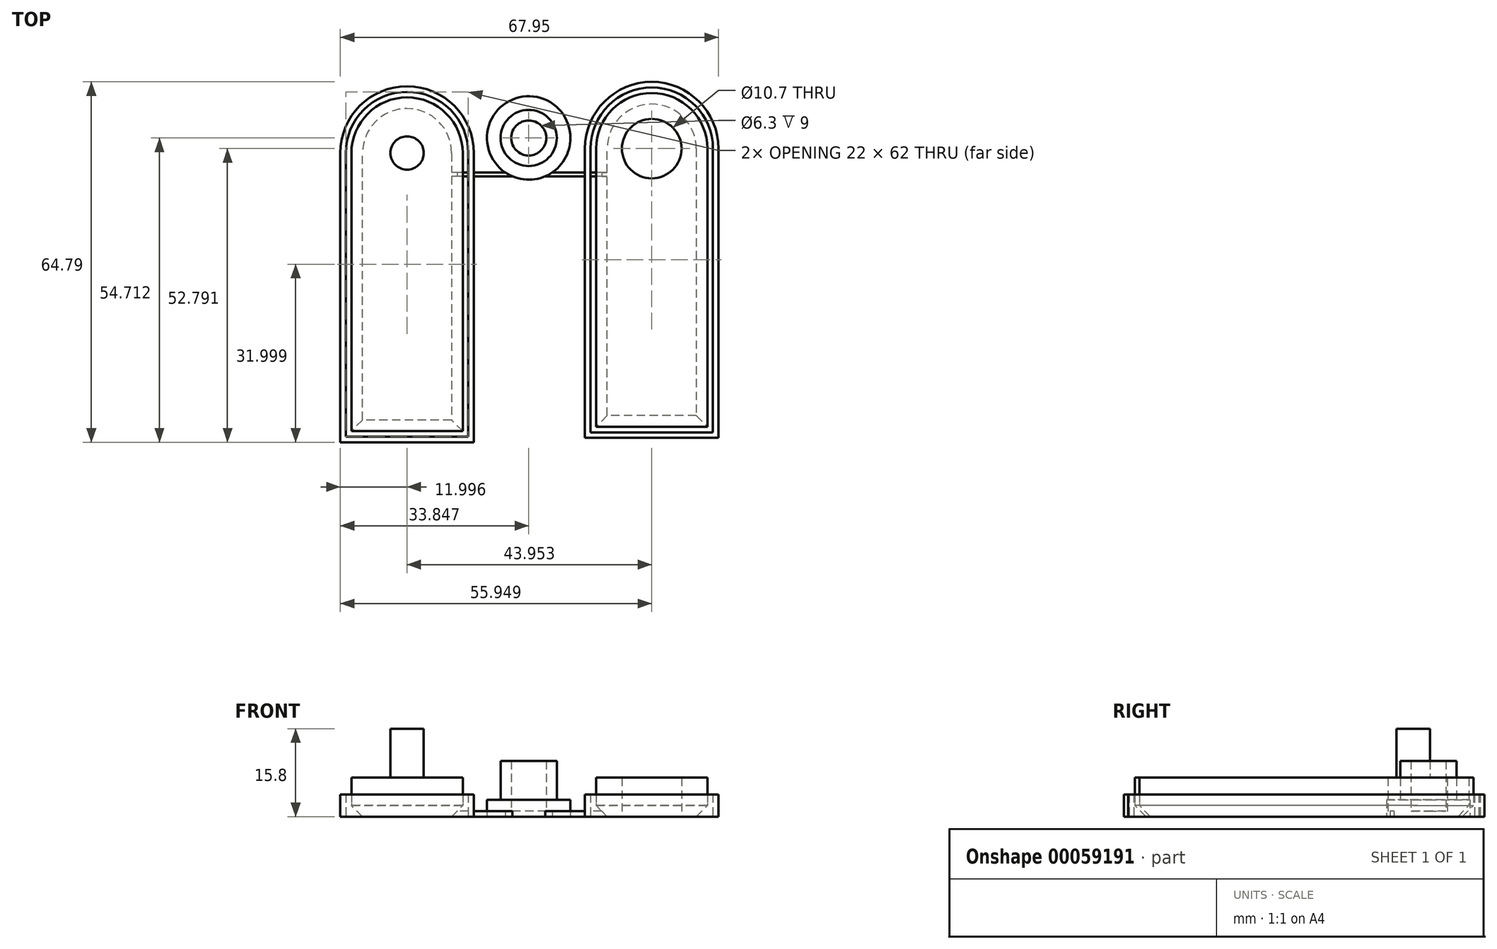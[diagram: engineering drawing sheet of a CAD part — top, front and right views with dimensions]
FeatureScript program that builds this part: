
annotation { "Feature Type Name" : "Feature", "Feature Type Description" : "" }
export const myFeature = defineFeature(function(context is Context, id is Id, definition is map)
    precondition{}
    {
        {
            assignVariable(context, id + "F0", {"name" : "heatWallThickness", "anyValue" : 4});
        }
        {
            var Q0;
            Q0=qCreatedBy(makeId("Top.planeOp"),FACE);
            var sketch = newSketch(context, id + "F1", { "sketchPlane" : qUnion([Q0])});
            skLineSegment(sketch, "E0.top", {"start": v(-67.54, 9.8) * mm, "end": v(-47.54, 9.8) * mm});
            skLineSegment(sketch, "E0.left", {"start": v(-67.54, 59.8) * mm, "end": v(-67.54, 9.8) * mm});
            skLineSegment(sketch, "E0.right", {"start": v(-47.54, 59.8) * mm, "end": v(-47.54, 9.8) * mm});
            skArc(sketch, "E1", {"start": v(-47.54, 59.8) * mm, "mid": v(-57.54, 69.8) * mm, "end": v(-67.54, 59.8) * mm});
            skCircle(sketch, "E2", {"center": v(-57.54, 59.8) * mm, "radius": 3 * mm});
            skLineSegment(sketch, "E3.left", {"start": v(-23.6, 60.6) * mm, "end": v(-23.6, 10.6) * mm});
            skCircle(sketch, "E4", {"center": v(-13.6, 60.6) * mm, "radius": 5.35 * mm});
            skArc(sketch, "E5", {"start": v(-3.6, 60.6) * mm, "mid": v(-13.6, 70.6) * mm, "end": v(-23.6, 60.6) * mm});
            skLineSegment(sketch, "E3.right", {"start": v(-3.6, 60.6) * mm, "end": v(-3.6, 10.6) * mm});
            skLineSegment(sketch, "E3.top", {"start": v(-23.6, 10.6) * mm, "end": v(-3.6, 10.6) * mm});
            skCircle(sketch, "E6", {"center": v(-35.7, 62.51) * mm, "radius": 7.5 * mm});
            skCircle(sketch, "E7", {"center": v(-35.7, 62.51) * mm, "radius": 5.05 * mm});
            skCircle(sketch, "E8", {"center": v(-35.7, 62.51) * mm, "radius": 3.15 * mm});
            skLineSegment(sketch, "E9.0", {"start": v(-46.54, 59.8) * mm, "end": v(-46.54, 8.8) * mm});
            skArc(sketch, "E9.1", {"start": v(-46.54, 59.8) * mm, "mid": v(-57.54, 70.8) * mm, "end": v(-68.54, 59.8) * mm});
            skLineSegment(sketch, "E9.2", {"start": v(-68.54, 59.8) * mm, "end": v(-68.54, 8.8) * mm});
            skLineSegment(sketch, "E9.3", {"start": v(-68.54, 8.8) * mm, "end": v(-46.54, 8.8) * mm});
            skLineSegment(sketch, "E10.0", {"start": v(-69.54, 7.8) * mm, "end": v(-45.54, 7.8) * mm});
            skLineSegment(sketch, "E10.1", {"start": v(-69.54, 59.8) * mm, "end": v(-69.54, 7.8) * mm});
            skArc(sketch, "E10.2", {"start": v(-45.54, 59.8) * mm, "mid": v(-57.54, 71.8) * mm, "end": v(-69.54, 59.8) * mm});
            skLineSegment(sketch, "E10.3", {"start": v(-45.54, 59.8) * mm, "end": v(-45.54, 7.8) * mm});
            skLineSegment(sketch, "E11.0", {"start": v(-24.6, 9.6) * mm, "end": v(-2.6, 9.6) * mm});
            skLineSegment(sketch, "E11.1", {"start": v(-24.6, 60.6) * mm, "end": v(-24.6, 9.6) * mm});
            skArc(sketch, "E11.2", {"start": v(-2.6, 60.6) * mm, "mid": v(-13.6, 71.6) * mm, "end": v(-24.6, 60.6) * mm});
            skLineSegment(sketch, "E11.3", {"start": v(-2.6, 60.6) * mm, "end": v(-2.6, 9.6) * mm});
            skLineSegment(sketch, "E12.0", {"start": v(-25.6, 8.6) * mm, "end": v(-1.6, 8.6) * mm});
            skLineSegment(sketch, "E12.1", {"start": v(-25.6, 60.6) * mm, "end": v(-25.6, 8.6) * mm});
            skArc(sketch, "E12.2", {"start": v(-1.6, 60.6) * mm, "mid": v(-13.6, 72.6) * mm, "end": v(-25.6, 60.6) * mm});
            skLineSegment(sketch, "E12.3", {"start": v(-1.6, 60.6) * mm, "end": v(-1.6, 8.6) * mm});
            skSolve(sketch);
        }
        {
            assignVariable(context, id + "F2", {"name" : "thickness", "anyValue" : 7 * mm});
        }
        {
            assignVariable(context, id + "F3", {"name" : "knobThickness", "anyValue" : 3 * mm});
        }
        {
            assignVariable(context, id + "F4", {"name" : "chamfer", "anyValue" : 2});
        }
        {
            var Q0;
            Q0=makeQuery(id+"F1.imprint","IMPRINT",FACE,{"disambiguationData":[TD([[makeQuery(id+"F1.imprint","IMPRINT",EDGE,{"derivedFrom":sQuery(id+"F1.wireOp",EDGE,"E0.top")}),1.0]])]});
            extrude(context, id + "F5", {"entities" : qUnion([Q0]), "depth" : getVariable(context, 'thickness')});
        }
        {
            var Q0;
            Q0=makeQuery(id+"F5.opExtrude","CAP_EDGE",EDGE,{"disambiguationData":[OSD([sQuery(id+"F1.wireOp",EDGE,"E0.top")])],"isStart":true});
            var Q1;
            Q1=makeQuery(id+"F5.opExtrude","CAP_EDGE",EDGE,{"disambiguationData":[OSD([sQuery(id+"F1.wireOp",EDGE,"E0.right")])],"isStart":true});
            var Q2;
            Q2=makeQuery(id+"F5.opExtrude","CAP_EDGE",EDGE,{"disambiguationData":[OSD([sQuery(id+"F1.wireOp",EDGE,"E1")])],"isStart":true});
            var Q3;
            Q3=makeQuery(id+"F5.opExtrude","CAP_EDGE",EDGE,{"disambiguationData":[OSD([sQuery(id+"F1.wireOp",EDGE,"E0.left")])],"isStart":true});
            chamfer(context, id + "F6", {"entities" : qUnion([Q0, Q1, Q2, Q3]), "width" : (getVariable(context, 'chamfer')) * mm, "tangentPropagation" : true});
        }
        {
            var Q0;
            Q0=makeQuery(id+"F1.imprint","IMPRINT",FACE,{"disambiguationData":[TD([[makeQuery(id+"F1.imprint","IMPRINT",EDGE,{"derivedFrom":sQuery(id+"F1.wireOp",EDGE,"E2")}),1.0]])]});
            extrude(context, id + "F7", {"entities" : qUnion([Q0]), "operationType" : NewBodyOperationType.ADD, "depth" : getVariable(context, 'thickness') + getVariable(context, 'thickness') + 1.8 * mm});
        }
        {
            var Q0;
            Q0=makeQuery(id+"F1.imprint","IMPRINT",FACE,{"disambiguationData":[TD([[makeQuery(id+"F1.imprint","IMPRINT",EDGE,{"derivedFrom":sQuery(id+"F1.wireOp",EDGE,"E3.left")}),1.0]])]});
            extrude(context, id + "F8", {"entities" : qUnion([Q0]), "depth" : getVariable(context, 'thickness')});
        }
        {
            var Q0;
            Q0=makeQuery(id+"F8.opExtrude","CAP_EDGE",EDGE,{"disambiguationData":[OSD([sQuery(id+"F1.wireOp",EDGE,"E3.top")])],"isStart":true});
            var Q1;
            Q1=makeQuery(id+"F8.opExtrude","CAP_EDGE",EDGE,{"disambiguationData":[OSD([sQuery(id+"F1.wireOp",EDGE,"E3.right")])],"isStart":true});
            var Q2;
            Q2=makeQuery(id+"F8.opExtrude","CAP_EDGE",EDGE,{"disambiguationData":[OSD([sQuery(id+"F1.wireOp",EDGE,"E5")])],"isStart":true});
            var Q3;
            Q3=makeQuery(id+"F8.opExtrude","CAP_EDGE",EDGE,{"disambiguationData":[OSD([sQuery(id+"F1.wireOp",EDGE,"E3.left")])],"isStart":true});
            chamfer(context, id + "F9", {"entities" : qUnion([Q0, Q1, Q2, Q3]), "width" : (getVariable(context, 'chamfer')) * mm, "tangentPropagation" : true});
        }
        {
            var Q0;
            Q0=makeQuery(id+"F1.imprint","IMPRINT",FACE,{"disambiguationData":[TD([[makeQuery(id+"F1.imprint","IMPRINT",EDGE,{"derivedFrom":sQuery(id+"F1.wireOp",EDGE,"E6")}),1.0]])]});
            extrude(context, id + "F10", {"entities" : qUnion([Q0]), "depth" : getVariable(context, 'knobThickness')});
        }
        {
            var Q0;
            Q0=makeQuery(id+"F1.imprint","IMPRINT",FACE,{"disambiguationData":[TD([[makeQuery(id+"F1.imprint","IMPRINT",EDGE,{"derivedFrom":sQuery(id+"F1.wireOp",EDGE,"E7")}),1.0]])]});
            extrude(context, id + "F11", {"entities" : qUnion([Q0]), "operationType" : NewBodyOperationType.ADD, "depth" : getVariable(context, 'thickness') + getVariable(context, 'knobThickness')});
        }
        {
            var Q0;
            Q0=makeQuery(id+"F1.imprint","IMPRINT",FACE,{"disambiguationData":[TD([[makeQuery(id+"F1.imprint","IMPRINT",EDGE,{"derivedFrom":sQuery(id+"F1.wireOp",EDGE,"E8")}),1.0]])]});
            extrude(context, id + "F12", {"entities" : qUnion([Q0]), "operationType" : NewBodyOperationType.ADD, "depth" : 1 * mm});
        }
        {
            var Q0;
            Q0=makeQuery(id+"F1.imprint","IMPRINT",FACE,{"disambiguationData":[TD([[makeQuery(id+"F1.imprint","IMPRINT",EDGE,{"derivedFrom":sQuery(id+"F1.wireOp",EDGE,"E9.0")}),1.0]])]});
            var Q1;
            Q1=makeQuery(id+"F1.imprint","IMPRINT",FACE,{"disambiguationData":[TD([[makeQuery(id+"F1.imprint","IMPRINT",EDGE,{"derivedFrom":sQuery(id+"F1.wireOp",EDGE,"E11.0")}),-1.0]])]});
            extrude(context, id + "F13", {"entities" : qUnion([Q0, Q1]), "depth" : (getVariable(context, 'heatWallThickness')) * mm});
        }
        {
            var Q0;
            Q0=qCreatedBy(makeId("Top.planeOp"),FACE);
            var sketch = newSketch(context, id + "F14", { "sketchPlane" : qUnion([Q0])});
            skLineSegment(sketch, "E13.rect.bottom", {"start": v(-16.96, 55.61) * mm, "end": v(-55.33, 55.61) * mm});
            skLineSegment(sketch, "E13.rect.top", {"start": v(-16.96, 56.3) * mm, "end": v(-55.33, 56.3) * mm});
            skLineSegment(sketch, "E13.rect.left", {"start": v(-16.96, 55.61) * mm, "end": v(-16.96, 56.3) * mm});
            skLineSegment(sketch, "E13.rect.right", {"start": v(-55.33, 55.61) * mm, "end": v(-55.33, 56.3) * mm});
            skPoint(sketch, "E13.rect.middle", {"position": v(-36.14, 55.96) * mm});
            skSolve(sketch);
        }
        {
            var Q0;
            Q0=makeQuery(id+"F14.imprint","IMPRINT",FACE,{"disambiguationData":[TD([[makeQuery(id+"F14.imprint","IMPRINT",EDGE,{"derivedFrom":sQuery(id+"F14.wireOp",EDGE,"E13.rect.bottom")}),-1.0]])]});
            extrude(context, id + "F15", {"entities" : qUnion([Q0]), "operationType" : NewBodyOperationType.ADD, "depth" : 1 * mm});
        }
    });
